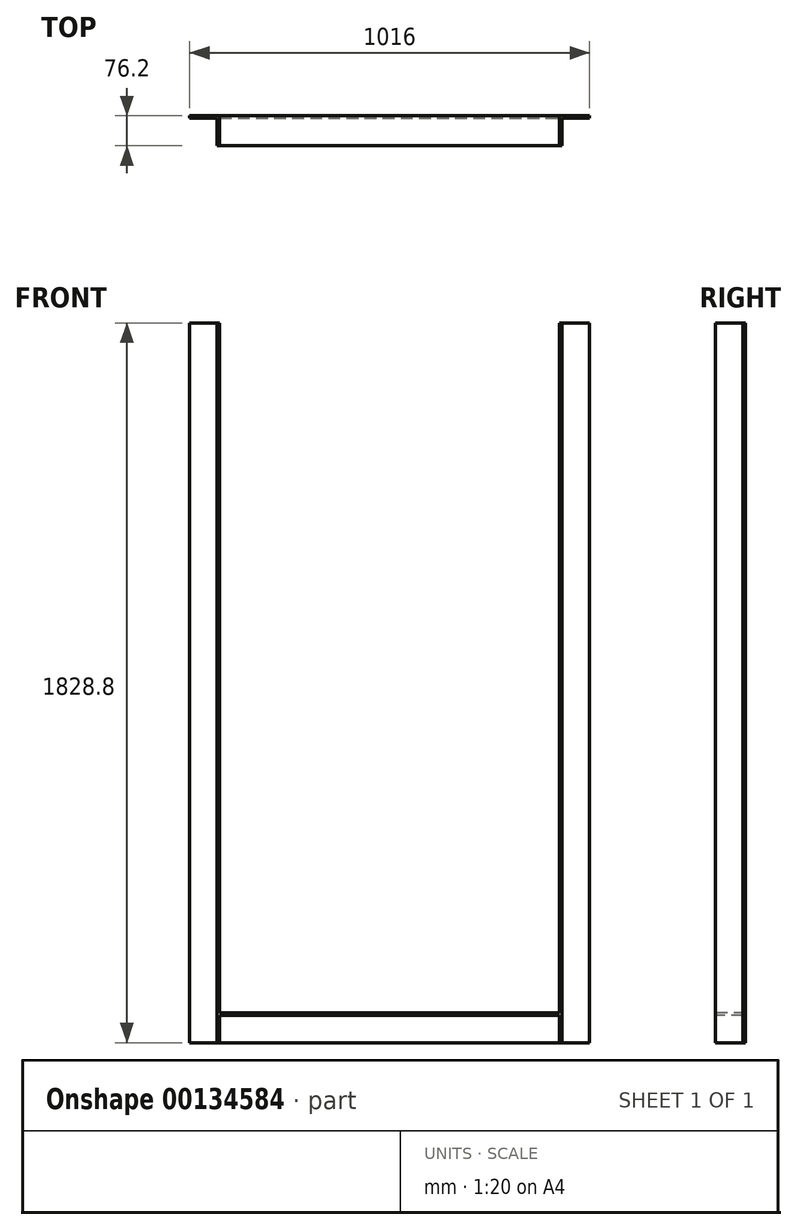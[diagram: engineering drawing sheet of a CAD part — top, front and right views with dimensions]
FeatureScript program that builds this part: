
annotation { "Feature Type Name" : "Feature", "Feature Type Description" : "" }
export const myFeature = defineFeature(function(context is Context, id is Id, definition is map)
    precondition{}
    {
        {
            var Q0;
            Q0=qCreatedBy(makeId("Top.planeOp"),FACE);
            var sketch = newSketch(context, id + "F0", { "sketchPlane" : qUnion([Q0])});
            skLineSegment(sketch, "E0.top", {"start": v(0, -76.2) * mm, "end": v(6.35, -76.2) * mm});
            skLineSegment(sketch, "E0.left", {"start": v(0, 0) * mm, "end": v(0, -76.2) * mm});
            skLineSegment(sketch, "E0.right", {"start": v(6.35, -6.35) * mm, "end": v(6.35, -76.2) * mm});
            skLineSegment(sketch, "E1.top", {"start": v(6.35, -6.35) * mm, "end": v(76.2, -6.35) * mm});
            skLineSegment(sketch, "E1.right", {"start": v(76.2, 0) * mm, "end": v(76.2, -6.35) * mm});
            skLineSegment(sketch, "E2", {"start": v(0, 0) * mm, "end": v(76.2, 0) * mm});
            skSolve(sketch);
        }
        {
            var Q0;
            Q0 = qSketchRegion(id + "F0", true);
            extrude(context, id + "F1", {"entities" : qUnion([Q0]), "depth" : 1828.8 * mm});
        }
        {
            var Q0;
            Q0=makeQuery(id+"F1.opExtrude","SWEPT_FACE",FACE,{"disambiguationData":[OSD([sQuery(id+"F0.wireOp",EDGE,"E0.left")])]});
            var sketch = newSketch(context, id + "F2", { "sketchPlane" : qUnion([Q0])});
            skLineSegment(sketch, "E3.bottom", {"start": v(0, 0) * mm, "end": v(6.35, 0) * mm});
            skLineSegment(sketch, "E3.left", {"start": v(0, 0) * mm, "end": v(0, 76.2) * mm});
            skLineSegment(sketch, "E4.top", {"start": v(6.35, 69.85) * mm, "end": v(76.2, 69.85) * mm});
            skLineSegment(sketch, "E4.right", {"start": v(76.2, 76.2) * mm, "end": v(76.2, 69.85) * mm});
            skLineSegment(sketch, "E5", {"start": v(6.35, 0) * mm, "end": v(6.35, 69.85) * mm});
            skLineSegment(sketch, "E6", {"start": v(0, 76.2) * mm, "end": v(76.2, 76.2) * mm});
            skSolve(sketch);
        }
        {
            var Q0;
            Q0 = qSketchRegion(id + "F2", true);
            extrude(context, id + "F3", {"entities" : qUnion([Q0]), "operationType" : NewBodyOperationType.ADD, "depth" : 431.8 * mm});
        }
        {
            var Q0;
            Q0=makeQuery(id+"F1.opExtrude","SWEPT_BODY",BODY,{"disambiguationData":[OSD([sQuery(id+"F0.wireOp",EDGE,"E0.top"),sQuery(id+"F0.wireOp",EDGE,"E0.left"),sQuery(id+"F0.wireOp",EDGE,"E0.right"),sQuery(id+"F0.wireOp",EDGE,"E1.top"),sQuery(id+"F0.wireOp",EDGE,"E1.right"),sQuery(id+"F0.wireOp",EDGE,"E2")])]});
            var Q1;
            Q1=makeQuery(id+"F3.opExtrude","CAP_FACE",FACE,{"disambiguationData":[OSD([sQuery(id+"F2.wireOp",EDGE,"E3.bottom"),sQuery(id+"F2.wireOp",EDGE,"E3.left"),sQuery(id+"F2.wireOp",EDGE,"E4.top"),sQuery(id+"F2.wireOp",EDGE,"E4.right"),sQuery(id+"F2.wireOp",EDGE,"E5"),sQuery(id+"F2.wireOp",EDGE,"E6")])],"isStart":false});
            mirror(context, id + "F4", {"operationType" : NewBodyOperationType.ADD, "entities" : qUnion([Q0]), "mirrorPlane" : qUnion([Q1])});
        }
    });
